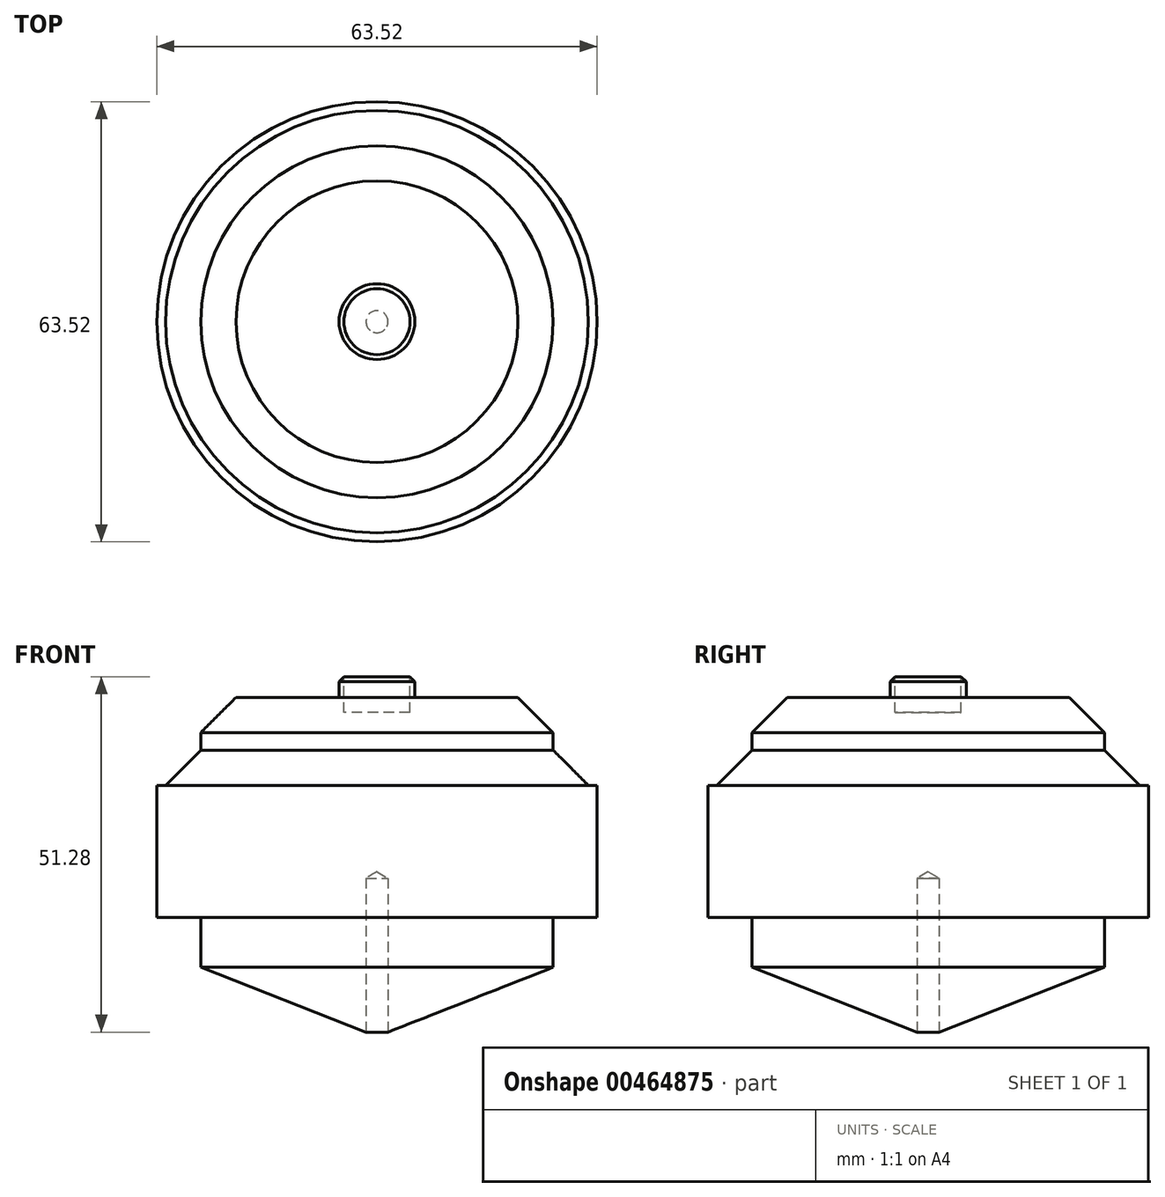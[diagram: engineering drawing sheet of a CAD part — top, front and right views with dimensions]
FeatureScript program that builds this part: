
annotation { "Feature Type Name" : "Feature", "Feature Type Description" : "" }
export const myFeature = defineFeature(function(context is Context, id is Id, definition is map)
    precondition{}
    {
        {
            var Q0;
            Q0=qCreatedBy(makeId("Front.planeOp"),FACE);
            var sketch = newSketch(context, id + "F0", { "sketchPlane" : qUnion([Q0])});
            skLineSegment(sketch, "E0.bottom", {"start": v(0, 56.27) * mm, "end": v(5.47, 56.27) * mm});
            skLineSegment(sketch, "E1", {"start": v(25.4, 48.94) * mm, "end": v(5.47, 48.94) * mm});
            skLineSegment(sketch, "E2", {"start": v(5.47, 48.94) * mm, "end": v(5.47, 56.27) * mm});
            skLineSegment(sketch, "E3", {"start": v(0, 56.27) * mm, "end": v(0, 0) * mm});
            skLineSegment(sketch, "E4", {"start": v(0, 0) * mm, "end": v(25.4, 9.96) * mm});
            skLineSegment(sketch, "E5", {"start": v(25.4, 48.94) * mm, "end": v(25.4, 36.24) * mm});
            skLineSegment(sketch, "E6", {"start": v(25.4, 17.2) * mm, "end": v(25.4, 9.96) * mm});
            skLineSegment(sketch, "E7", {"start": v(25.4, 36.24) * mm, "end": v(31.76, 36.24) * mm});
            skLineSegment(sketch, "E8", {"start": v(31.76, 36.24) * mm, "end": v(31.76, 17.2) * mm});
            skLineSegment(sketch, "E9", {"start": v(31.76, 17.2) * mm, "end": v(25.4, 17.2) * mm});
            skSolve(sketch);
        }
        {
            var Q0;
            Q0=makeQuery(id+"F0.imprint","IMPRINT",FACE,{"disambiguationData":[TD([[makeQuery(id+"F0.imprint","IMPRINT",EDGE,{"derivedFrom":sQuery(id+"F0.wireOp",EDGE,"E0.bottom")}),-1.0]])]});
            var Q1;
            Q1=sQuery(id+"F0.wireOp",EDGE,"E3");
            revolve(context, id + "F1", {"entities" : qUnion([Q0]), "axis" : qUnion([Q1]), "revolveType" : RevolveType.FULL});
        }
        {
            var Q0;
            Q0=makeQuery(id+"F1.opRevolve","SWEPT_FACE",FACE,{"disambiguationData":[OSD([sQuery(id+"F0.wireOp",EDGE,"E0.bottom")])]});
            var sketch = newSketch(context, id + "F2", { "sketchPlane" : qUnion([Q0])});
            skCircle(sketch, "E10", {"center": v(0, 0) * mm, "radius": 4.76 * mm});
            skSolve(sketch);
        }
        {
            var Q0;
            Q0=makeQuery(id+"F2.imprint","IMPRINT",FACE,{"disambiguationData":[TD([[makeQuery(id+"F2.imprint","IMPRINT",EDGE,{"derivedFrom":sQuery(id+"F2.wireOp",EDGE,"E10")}),1.0]])]});
            var Q1;
            Q1=sQuery(id+"F2.wireOp",EDGE,"E10");
            extrude(context, id + "F3", {"entities" : qUnion([Q0]), "operationType" : NewBodyOperationType.REMOVE, "surfaceEntities" : qUnion([Q1]), "oppositeDirection" : true, "depth" : 9.52 * mm});
        }
        {
            var Q0;
            Q0=makeQuery(id+"F1.opRevolve","SWEPT_EDGE",EDGE,{"disambiguationData":[OSD([sQuery(id+"F0.wireOp",EDGE,"E0.bottom"),sQuery(id+"F0.wireOp",EDGE,"E2")])]});
            chamfer(context, id + "F4", {"entities" : qUnion([Q0]), "width" : 5.08 * mm, "tangentPropagation" : true});
        }
        {
            var Q0;
            Q0=qCreatedBy(makeId("Top.planeOp"),FACE);
            var sketch = newSketch(context, id + "F5", { "sketchPlane" : qUnion([Q0])});
            skCircle(sketch, "E11", {"center": v(0, 0) * mm, "radius": 1.59 * mm});
            skSolve(sketch);
        }
        {
            var Q0;
            Q0=sQuery(id+"F5.wireOp",VERTEX,"E11.center");
            var Q1;
            Q1=makeQuery(id+"F1.opRevolve","SWEPT_BODY",BODY,{"disambiguationData":[OSD([sQuery(id+"F0.wireOp",EDGE,"E0.bottom"),sQuery(id+"F0.wireOp",EDGE,"nVd5dQAl-Cuxq-WPEE-NKpS-jWTfpGOwdUjI"),sQuery(id+"F0.wireOp",EDGE,"VJVXweN1-2UXW-E2JH-iOqI-g908Ri4Z09Hg"),sQuery(id+"F0.wireOp",EDGE,"E1"),sQuery(id+"F0.wireOp",EDGE,"E2"),sQuery(id+"F0.wireOp",EDGE,"E3")])]});
            hole(context, id + "F6", {"style" : HoleStyle.SIMPLE, "endStyle" : HoleEndStyle.BLIND, "oppositeDirection" : true, "holeDiameter" : 3.17 * mm, "holeDepth" : 22.22 * mm, "isTappedThrough" : true, "tappedDepth" : 12.7 * mm, "tapClearance" : 3, "locations" : qUnion([Q0]), "scope" : qUnion([Q1])});
        }
        {
            var Q0;
            Q0=makeQuery(id+"F1.opRevolve","SWEPT_FACE",FACE,{"disambiguationData":[OSD([sQuery(id+"F0.wireOp",EDGE,"E5")])]});
            chamfer(context, id + "F7", {"entities" : qUnion([Q0]), "width" : 5.08 * mm, "tangentPropagation" : true});
        }
    });
